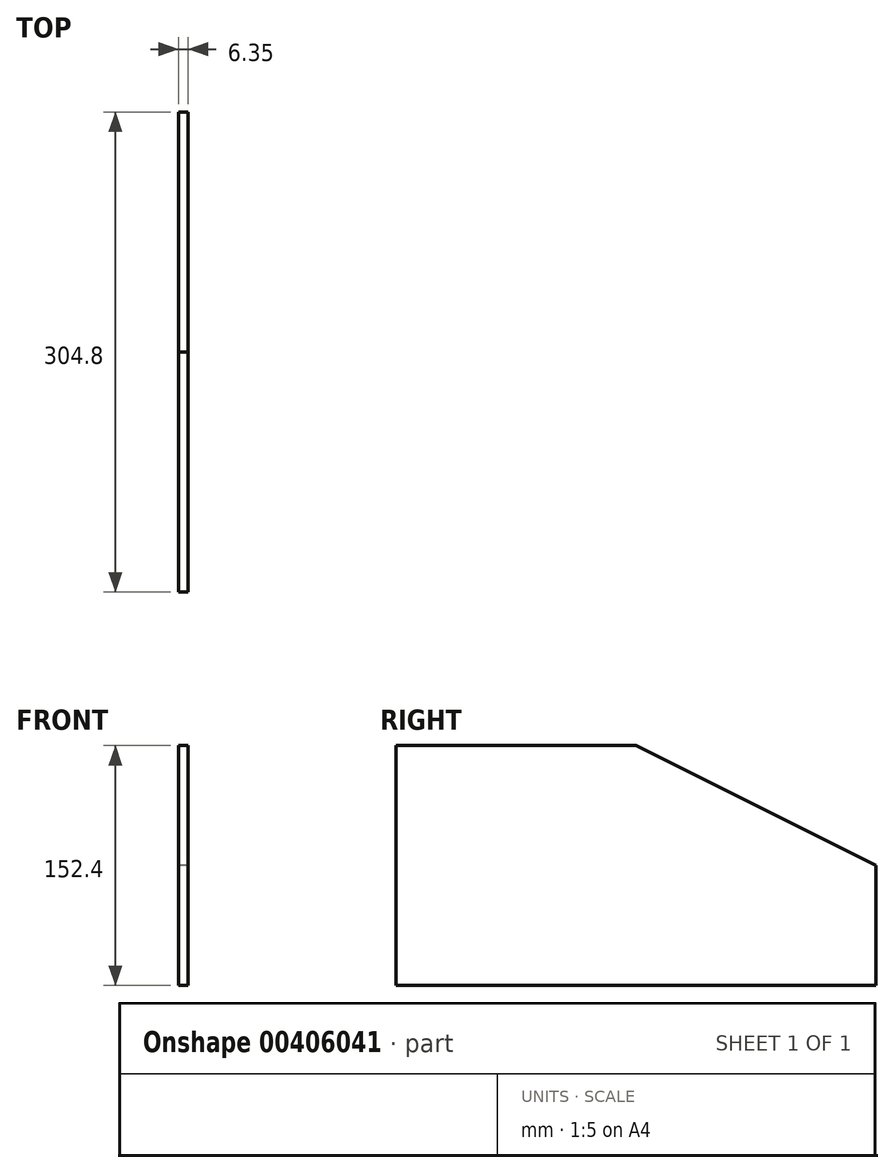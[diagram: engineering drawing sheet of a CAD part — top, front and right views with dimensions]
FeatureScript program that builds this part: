
annotation { "Feature Type Name" : "Feature", "Feature Type Description" : "" }
export const myFeature = defineFeature(function(context is Context, id is Id, definition is map)
    precondition{}
    {
        {
            var Q0;
            Q0=qCreatedBy(makeId("Right.planeOp"),FACE);
            var sketch = newSketch(context, id + "F0", { "sketchPlane" : qUnion([Q0])});
            skLineSegment(sketch, "E0.bottom", {"start": v(152.4, -76.2) * mm, "end": v(-152.4, -76.2) * mm});
            skLineSegment(sketch, "E0.top", {"start": v(0, 76.2) * mm, "end": v(-152.4, 76.2) * mm});
            skLineSegment(sketch, "E0.left", {"start": v(152.4, -76.2) * mm, "end": v(152.4, 0) * mm});
            skLineSegment(sketch, "E0.right", {"start": v(-152.4, -76.2) * mm, "end": v(-152.4, 76.2) * mm});
            skPoint(sketch, "E0.middle", {"position": v(0, 0) * mm});
            skLineSegment(sketch, "E1", {"start": v(0, 76.2) * mm, "end": v(152.4, 0) * mm});
            skPoint(sketch, "E2.orphan", {"position": v(152.4, 76.2) * mm});
            skSolve(sketch);
        }
        {
            var Q0;
            Q0 = qSketchRegion(id + "F0", true);
            extrude(context, id + "F1", {"entities" : qUnion([Q0]), "depth" : 6.35 * mm});
        }
    });
